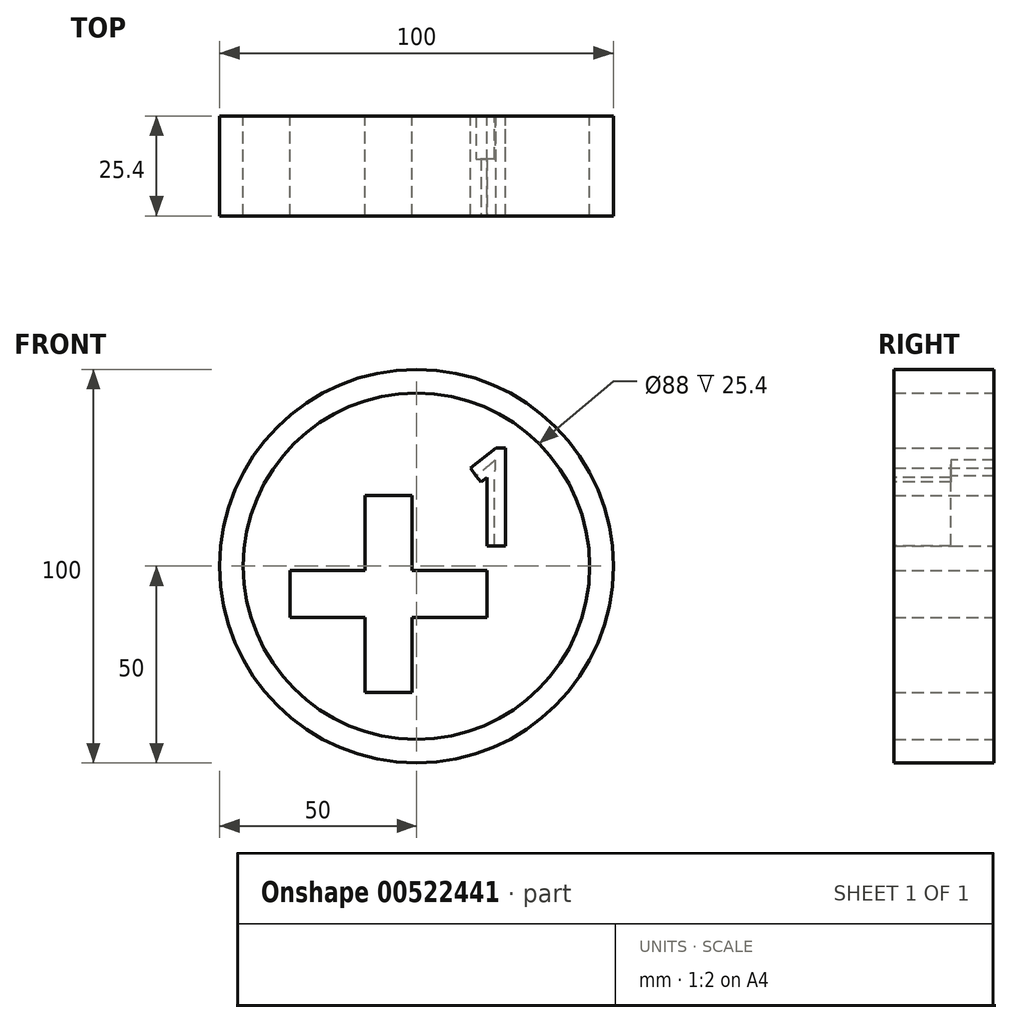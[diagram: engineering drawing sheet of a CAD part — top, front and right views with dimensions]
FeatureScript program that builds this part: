
annotation { "Feature Type Name" : "Feature", "Feature Type Description" : "" }
export const myFeature = defineFeature(function(context is Context, id is Id, definition is map)
    precondition{}
    {
        {
            var Q0;
            Q0=qCreatedBy(makeId("Front.planeOp"),FACE);
            var sketch = newSketch(context, id + "F0", { "sketchPlane" : qUnion([Q0])});
            skCircle(sketch, "E0", {"center": v(0, 0) * mm, "radius": 50 * mm});
            skCircle(sketch, "E1", {"center": v(0, 0) * mm, "radius": 44 * mm});
            skPoint(sketch, "E2", {"position": v(0, -50) * mm});
            skText(sketch, "E3", { "text": "1", "fontName": "OpenSans-Regular.ttf"});
            skLineSegment(sketch, "E4", {"start": v(0, 0) * mm, "end": v(17.68, 17.68) * mm});
            skLineSegment(sketch, "E5", {"start": v(0, 0) * mm, "end": v(5.66, 0) * mm});
            skLineSegment(sketch, "E6.bottom", {"start": v(-1.07, -32.07) * mm, "end": v(-13.07, -32.07) * mm});
            skLineSegment(sketch, "E6.top", {"start": v(-1.07, 17.93) * mm, "end": v(-13.07, 17.93) * mm});
            skLineSegment(sketch, "E6.left", {"start": v(-1.07, -32.07) * mm, "end": v(-1.07, 17.93) * mm});
            skLineSegment(sketch, "E6.right", {"start": v(-13.07, -32.07) * mm, "end": v(-13.07, 17.93) * mm});
            skPoint(sketch, "E6.middle", {"position": v(-7.07, -7.07) * mm});
            skLineSegment(sketch, "E7.bottom", {"start": v(17.93, -13.07) * mm, "end": v(-32.07, -13.07) * mm});
            skLineSegment(sketch, "E7.top", {"start": v(17.93, -1.07) * mm, "end": v(-32.07, -1.07) * mm});
            skLineSegment(sketch, "E7.left", {"start": v(17.93, -13.07) * mm, "end": v(17.93, -1.07) * mm});
            skLineSegment(sketch, "E7.right", {"start": v(-32.07, -13.07) * mm, "end": v(-32.07, -1.07) * mm});
            skLineSegment(sketch, "E8", {"start": v(-7.07, -7.07) * mm, "end": v(0, 0) * mm});
            const initialGuessF0  = {"E3": [0.0105, 0.00518, 1, 0, 0.025]};
            skSetInitialGuess(sketch, initialGuessF0);
            skSolve(sketch);
        }
        {
            var Q0;
            Q0=makeQuery(id+"F0.imprint","IMPRINT",FACE,{"disambiguationData":[TD([[makeQuery(id+"F0.imprint","IMPRINT",EDGE,{"derivedFrom":sQuery(id+"F0.wireOp",EDGE,"E0")}),1.0]])]});
            var Q1;
            {var subQ9=sQuery(id+"F0.wireOp",EDGE,"JPuuaeZV-5oA1-bOET-emPB-8E9oC848Bjk7");Q1=makeQuery(id+"F0.imprint","IMPRINT",FACE,{"disambiguationData":[TD([[makeQuery(id+"F0.imprint","IMPRINT",EDGE,{"derivedFrom":subQ9}),1.0]])]});}
            var Q2;
            {var subQ1=sQuery(id+"F0.wireOp",EDGE,"1czAJEjm-GAaO-qJbW-bNPJ-VOC9MhbBWLXS");var subQ3=sQuery(id+"F0.wireOp",EDGE,"90a05c53-9c47-40ab-b859-f5c182912d02.1");var subQ4=makeQuery(id+"F0.imprint","INTERSECT",VERTEX,{"derivedFrom":[subQ1,subQ3]});Q2=makeQuery(id+"F0.imprint","IMPRINT",FACE,{"disambiguationData":[TD([[makeQuery(id+"F0.imprint","IMPRINT",EDGE,{"disambiguationData":[TD([[subQ4,-1.0]])],"derivedFrom":subQ3}),1.0]])]});}
            extrude(context, id + "F1", {"entities" : qUnion([Q0, Q1, Q2]), "depth" : 25.4 * mm});
        }
        {
            var Q0;
            {var subQ0=sQuery(id+"F0.wireOp",EDGE,"E7.bottom");var subQ1=sQuery(id+"F0.wireOp",EDGE,"E6.left");var subQ2=makeQuery(id+"F0.imprint","INTERSECT",VERTEX,{"derivedFrom":[subQ1,subQ0]});Q0=makeQuery(id+"F0.imprint","IMPRINT",FACE,{"disambiguationData":[TD([[makeQuery(id+"F0.imprint","IMPRINT",EDGE,{"disambiguationData":[TD([[subQ2,-1.0]])],"derivedFrom":subQ1}),1.0]])]});}
            var Q1;
            {var subQ5=sQuery(id+"F0.wireOp",EDGE,"E7.right");Q1=makeQuery(id+"F0.imprint","IMPRINT",FACE,{"disambiguationData":[TD([[makeQuery(id+"F0.imprint","IMPRINT",EDGE,{"derivedFrom":subQ5}),-1.0]])]});}
            var Q2;
            {var subQ5=sQuery(id+"F0.wireOp",EDGE,"E7.left");Q2=makeQuery(id+"F0.imprint","IMPRINT",FACE,{"disambiguationData":[TD([[makeQuery(id+"F0.imprint","IMPRINT",EDGE,{"derivedFrom":subQ5}),1.0]])]});}
            var Q3;
            {var subQ0=sQuery(id+"F0.wireOp",EDGE,"E6.bottom");Q3=makeQuery(id+"F0.imprint","IMPRINT",FACE,{"disambiguationData":[TD([[makeQuery(id+"F0.imprint","IMPRINT",EDGE,{"derivedFrom":subQ0}),-1.0]])]});}
            var Q4;
            {var subQ0=sQuery(id+"F0.wireOp",EDGE,"E6.top");Q4=makeQuery(id+"F0.imprint","IMPRINT",FACE,{"disambiguationData":[TD([[makeQuery(id+"F0.imprint","IMPRINT",EDGE,{"derivedFrom":subQ0}),1.0]])]});}
            var Q5;
            Q5=makeQuery(id+"F0.imprint","IMPRINT",FACE,{"disambiguationData":[TD([[makeQuery(id+"F0.imprint","IMPRINT",EDGE,{"derivedFrom":sQuery(id+"F0.wireOp",EDGE,"E3.sketch_text.stroke-0")}),-1.0]])]});
            extrude(context, id + "F2", {"entities" : qUnion([Q0, Q1, Q2, Q3, Q4, Q5]), "depth" : 25.4 * mm, "offsetDistance" : 25.4 * mm});
        }
        {
            var Q0;
            Q0=makeQuery(id+"F2.opExtrude","CAP_FACE",FACE,{"disambiguationData":[OSD([sQuery(id+"F0.wireOp",EDGE,"E3.sketch_text.stroke-0"),sQuery(id+"F0.wireOp",EDGE,"E3.sketch_text.stroke-1"),sQuery(id+"F0.wireOp",EDGE,"E3.sketch_text.stroke-2"),sQuery(id+"F0.wireOp",EDGE,"E3.sketch_text.stroke-3"),sQuery(id+"F0.wireOp",EDGE,"E3.sketch_text.stroke-4"),sQuery(id+"F0.wireOp",EDGE,"E3.sketch_text.stroke-5"),sQuery(id+"F0.wireOp",EDGE,"E3.sketch_text.stroke-6"),sQuery(id+"F0.wireOp",EDGE,"E3.sketch_text.stroke-7"),sQuery(id+"F0.wireOp",EDGE,"E3.sketch_text.stroke-8")])],"isStart":false});
            var sketch = newSketch(context, id + "F3", { "sketchPlane" : qUnion([Q0])});
            skLineSegment(sketch, "E9", {"start": v(19.87, 5.18) * mm, "end": v(17.87, 5.18) * mm});
            skLineSegment(sketch, "E10", {"start": v(17.87, 5.18) * mm, "end": v(17.87, 25.16) * mm});
            skLineSegment(sketch, "E11", {"start": v(17.87, 25.16) * mm, "end": v(20.65, 28.63) * mm});
            skLineSegment(sketch, "E12", {"start": v(20.65, 28.63) * mm, "end": v(22.61, 5.18) * mm});
            skLineSegment(sketch, "E13", {"start": v(22.61, 5.18) * mm, "end": v(17.87, 5.18) * mm});
            skLineSegment(sketch, "E14", {"start": v(15.17, 22.96) * mm, "end": v(16.4, 21.38) * mm});
            skLineSegment(sketch, "E15", {"start": v(16.4, 21.38) * mm, "end": v(19.88, 24.07) * mm});
            skLineSegment(sketch, "E16", {"start": v(15.17, 22.96) * mm, "end": v(20, 27.01) * mm});
            skSolve(sketch);
        }
        {
            var Q0;
            Q0 = qSketchRegion(id + "F3", true);
            extrude(context, id + "F4", {"entities" : qUnion([Q0]), "operationType" : NewBodyOperationType.ADD, "oppositeDirection" : true, "depth" : 14.48 * mm, "offsetDistance" : 25.4 * mm});
        }
    });
